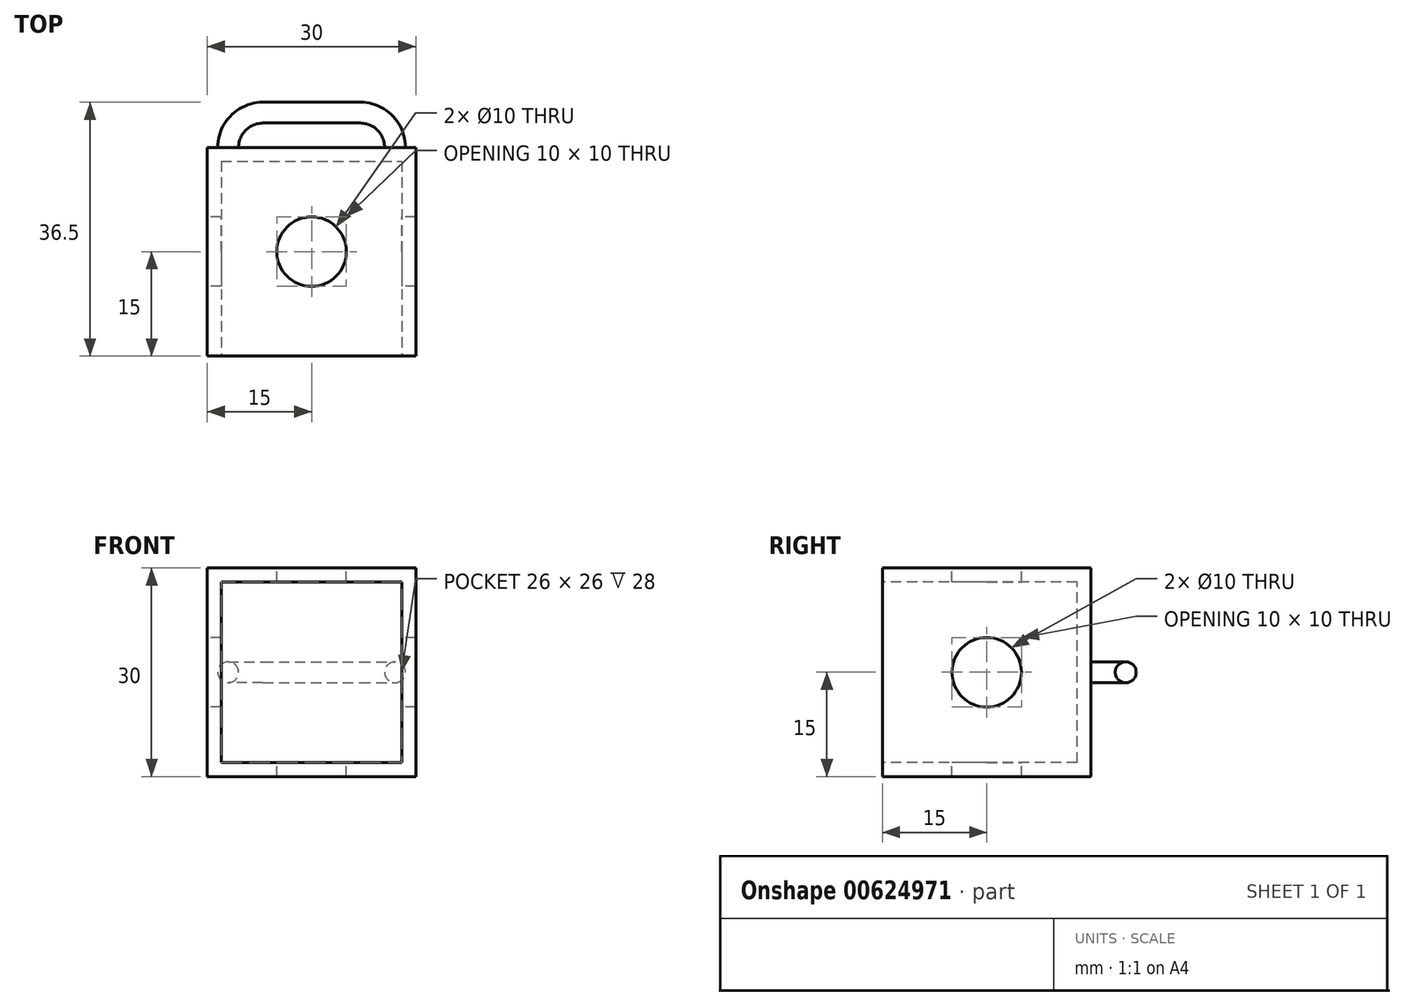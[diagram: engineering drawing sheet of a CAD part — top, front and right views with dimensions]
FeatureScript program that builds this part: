
annotation { "Feature Type Name" : "Feature", "Feature Type Description" : "" }
export const myFeature = defineFeature(function(context is Context, id is Id, definition is map)
    precondition{}
    {
        {
            var Q0;
            Q0=qCreatedBy(makeId("Top.planeOp"),FACE);
            var sketch = newSketch(context, id + "F0", { "sketchPlane" : qUnion([Q0])});
            skLineSegment(sketch, "E0.bottom", {"start": v(0, 0) * mm, "end": v(30, 0) * mm});
            skLineSegment(sketch, "E0.top", {"start": v(0, 30) * mm, "end": v(30, 30) * mm});
            skLineSegment(sketch, "E0.left", {"start": v(0, 0) * mm, "end": v(0, 30) * mm});
            skLineSegment(sketch, "E0.right", {"start": v(30, 0) * mm, "end": v(30, 30) * mm});
            skSolve(sketch);
        }
        {
            var Q0;
            Q0 = qSketchRegion(id + "F0", true);
            extrude(context, id + "F1", {"entities" : qUnion([Q0]), "depth" : 30 * mm, "offsetDistance" : 25 * mm});
        }
        {
            var Q0;
            Q0=makeQuery(id+"F1.opExtrude","SWEPT_FACE",FACE,{"disambiguationData":[OSD([sQuery(id+"F0.wireOp",EDGE,"E0.top")])]});
            var sketch = newSketch(context, id + "F2", { "sketchPlane" : qUnion([Q0])});
            skLineSegment(sketch, "E1", {"start": v(0, 15) * mm, "end": v(-30, 15) * mm, "construction": true});
            skSolve(sketch);
        }
        {
            var Q0;
            Q0=sQuery(id+"F2.wireOp",EDGE,"E1");
            var Q1;
            Q1=qCreatedBy(makeId("Front.planeOp"),FACE);
            cPlane(context, id + "F3", {"entities" : qUnion([Q0, Q1]), "cplaneType" : CPlaneType.LINE_ANGLE, "offset" : 15 * mm, "angle" : 90 * degree, "oppositeDirection" : true, "width" : 150 * mm, "height" : 150 * mm});
        }
        {
            var Q0;
            Q0=qCreatedBy(id+"F3.planeOp",FACE);
            var sketch = newSketch(context, id + "F4", { "sketchPlane" : qUnion([Q0])});
            skArc(sketch, "E2", {"start": v(3, -30) * mm, "mid": v(4.46, -33.54) * mm, "end": v(8, -35) * mm});
            skArc(sketch, "E3", {"start": v(22, -35) * mm, "mid": v(25.54, -33.54) * mm, "end": v(27, -30) * mm});
            skLineSegment(sketch, "E4", {"start": v(8, -35) * mm, "end": v(22, -35) * mm});
            skSolve(sketch);
        }
        {
            var Q0;
            {var subQ0=sQuery(id+"F0.wireOp",EDGE,"E0.top");Q0=makeQuery(id+"F2.imprint","IMPRINT",FACE,{"disambiguationData":[TD([[makeQuery(id+"F2.imprint","IMPRINT",EDGE,{"derivedFrom":makeQuery(id+"F1.opExtrude","CAP_EDGE",EDGE,{"disambiguationData":[OSD([subQ0])],"isStart":true})}),-1.0]])]});}
            var sketch = newSketch(context, id + "F5", { "sketchPlane" : qUnion([Q0])});
            skCircle(sketch, "E5", {"center": v(-3, 15) * mm, "radius": 1.5 * mm});
            skCircle(sketch, "E6", {"center": v(-26.94, 14.8) * mm, "radius": 1.5 * mm});
            skSolve(sketch);
        }
        {
            var Q0;
            Q0=makeQuery(id+"F5.imprint","IMPRINT",FACE,{"disambiguationData":[TD([[makeQuery(id+"F5.imprint","IMPRINT",EDGE,{"derivedFrom":sQuery(id+"F5.wireOp",EDGE,"E5")}),1.0]])]});
            var Q1;
            Q1 = qConstructionFilter(qBodyType(qCreatedBy(id + "F4" ,EDGE), BodyType.WIRE), ConstructionObject.NO);
            sweep(context, id + "F6", {"operationType" : NewBodyOperationType.ADD, "profiles" : qUnion([Q0]), "path" : qUnion([Q1])});
        }
        {
            var Q0;
            Q0=makeQuery(id+"F1.opExtrude","SWEPT_FACE",FACE,{"disambiguationData":[OSD([sQuery(id+"F0.wireOp",EDGE,"E0.bottom")])]});
            var sketch = newSketch(context, id + "F7", { "sketchPlane" : qUnion([Q0])});
            skLineSegment(sketch, "E7.bottom", {"start": v(2, 2) * mm, "end": v(28, 2) * mm});
            skLineSegment(sketch, "E7.top", {"start": v(2, 28) * mm, "end": v(28, 28) * mm});
            skLineSegment(sketch, "E7.left", {"start": v(2, 2) * mm, "end": v(2, 28) * mm});
            skLineSegment(sketch, "E7.right", {"start": v(28, 2) * mm, "end": v(28, 28) * mm});
            skPoint(sketch, "E7.middle", {"position": v(15, 15) * mm});
            skLineSegment(sketch, "E8", {"start": v(15, 15) * mm, "end": v(15, 0) * mm, "construction": true});
            skLineSegment(sketch, "E9", {"start": v(15, 15) * mm, "end": v(0, 15) * mm, "construction": true});
            skSolve(sketch);
        }
        {
            var Q0;
            Q0=makeQuery(id+"F7.imprint","IMPRINT",FACE,{"disambiguationData":[TD([[makeQuery(id+"F7.imprint","IMPRINT",EDGE,{"derivedFrom":sQuery(id+"F7.wireOp",EDGE,"E7.bottom")}),1.0]])]});
            var Q1;
            Q1=makeQuery(id+"F1.opExtrude","SWEPT_FACE",FACE,{"disambiguationData":[OSD([sQuery(id+"F0.wireOp",EDGE,"E0.top")])]});
            extrude(context, id + "F8", {"entities" : qUnion([Q0]), "operationType" : NewBodyOperationType.REMOVE, "endBound" : BoundingType.UP_TO_SURFACE, "oppositeDirection" : true, "depth" : 25 * mm, "endBoundEntityFace" : qUnion([Q1]), "offsetDistance" : 25 * mm});
        }
        {
            var Q0;
            {var subQ0=sQuery(id+"F0.wireOp",EDGE,"E0.top");Q0=makeQuery(id+"F2.imprint","IMPRINT",FACE,{"disambiguationData":[TD([[makeQuery(id+"F2.imprint","IMPRINT",EDGE,{"derivedFrom":makeQuery(id+"F1.opExtrude","CAP_EDGE",EDGE,{"disambiguationData":[OSD([subQ0])],"isStart":true})}),-1.0]])]});}
            var sketch = newSketch(context, id + "F9", { "sketchPlane" : qUnion([Q0])});
            skLineSegment(sketch, "E10.bottom", {"start": v(0, 0) * mm, "end": v(-30, 0) * mm});
            skLineSegment(sketch, "E10.top", {"start": v(0, 30) * mm, "end": v(-30, 30) * mm});
            skLineSegment(sketch, "E10.left", {"start": v(0, 0) * mm, "end": v(0, 30) * mm});
            skLineSegment(sketch, "E10.right", {"start": v(-30, 0) * mm, "end": v(-30, 30) * mm});
            skSolve(sketch);
        }
        {
            var Q0;
            Q0 = qSketchRegion(id + "F9", true);
            extrude(context, id + "F10", {"entities" : qUnion([Q0]), "operationType" : NewBodyOperationType.ADD, "oppositeDirection" : true, "depth" : 2 * mm, "offsetDistance" : 25 * mm});
        }
        {
            var Q0;
            Q0=makeQuery(id+"F1.opExtrude","CAP_FACE",FACE,{"disambiguationData":[OSD([sQuery(id+"F0.wireOp",EDGE,"E0.bottom"),sQuery(id+"F0.wireOp",EDGE,"E0.top"),sQuery(id+"F0.wireOp",EDGE,"E0.left"),sQuery(id+"F0.wireOp",EDGE,"E0.right")])],"isStart":false});
            var sketch = newSketch(context, id + "F11", { "sketchPlane" : qUnion([Q0])});
            skCircle(sketch, "E11", {"center": v(15, 15) * mm, "radius": 5 * mm});
            skLineSegment(sketch, "E12", {"start": v(15, 15) * mm, "end": v(15, 30) * mm, "construction": true});
            skLineSegment(sketch, "E13", {"start": v(15, 15) * mm, "end": v(15, 0) * mm, "construction": true});
            skSolve(sketch);
        }
        {
            var Q0;
            Q0=makeQuery(id+"F11.imprint","IMPRINT",FACE,{"disambiguationData":[TD([[makeQuery(id+"F11.imprint","IMPRINT",EDGE,{"derivedFrom":sQuery(id+"F11.wireOp",EDGE,"E11")}),1.0]])]});
            var Q1;
            Q1=makeQuery(id+"F1.opExtrude","CAP_FACE",FACE,{"disambiguationData":[OSD([sQuery(id+"F0.wireOp",EDGE,"E0.bottom"),sQuery(id+"F0.wireOp",EDGE,"E0.top"),sQuery(id+"F0.wireOp",EDGE,"E0.left"),sQuery(id+"F0.wireOp",EDGE,"E0.right")])],"isStart":true});
            extrude(context, id + "F12", {"entities" : qUnion([Q0]), "operationType" : NewBodyOperationType.REMOVE, "endBound" : BoundingType.UP_TO_SURFACE, "oppositeDirection" : true, "depth" : 25 * mm, "endBoundEntityFace" : qUnion([Q1]), "offsetDistance" : 25 * mm});
        }
        {
            var Q0;
            Q0=makeQuery(id+"F1.opExtrude","SWEPT_FACE",FACE,{"disambiguationData":[OSD([sQuery(id+"F0.wireOp",EDGE,"E0.left")])]});
            var sketch = newSketch(context, id + "F13", { "sketchPlane" : qUnion([Q0])});
            skCircle(sketch, "E14", {"center": v(-15, 15) * mm, "radius": 5 * mm});
            skLineSegment(sketch, "E15", {"start": v(-15, 15) * mm, "end": v(-30, 15) * mm, "construction": true});
            skLineSegment(sketch, "E16", {"start": v(-15, 15) * mm, "end": v(0, 15) * mm, "construction": true});
            skSolve(sketch);
        }
        {
            var Q0;
            Q0=makeQuery(id+"F13.imprint","IMPRINT",FACE,{"disambiguationData":[TD([[makeQuery(id+"F13.imprint","IMPRINT",EDGE,{"derivedFrom":sQuery(id+"F13.wireOp",EDGE,"E14")}),1.0]])]});
            var Q1;
            Q1=makeQuery(id+"F1.opExtrude","SWEPT_FACE",FACE,{"disambiguationData":[OSD([sQuery(id+"F0.wireOp",EDGE,"E0.right")])]});
            extrude(context, id + "F14", {"entities" : qUnion([Q0]), "operationType" : NewBodyOperationType.REMOVE, "endBound" : BoundingType.UP_TO_SURFACE, "oppositeDirection" : true, "depth" : 25 * mm, "endBoundEntityFace" : qUnion([Q1]), "offsetDistance" : 25 * mm});
        }
    });
